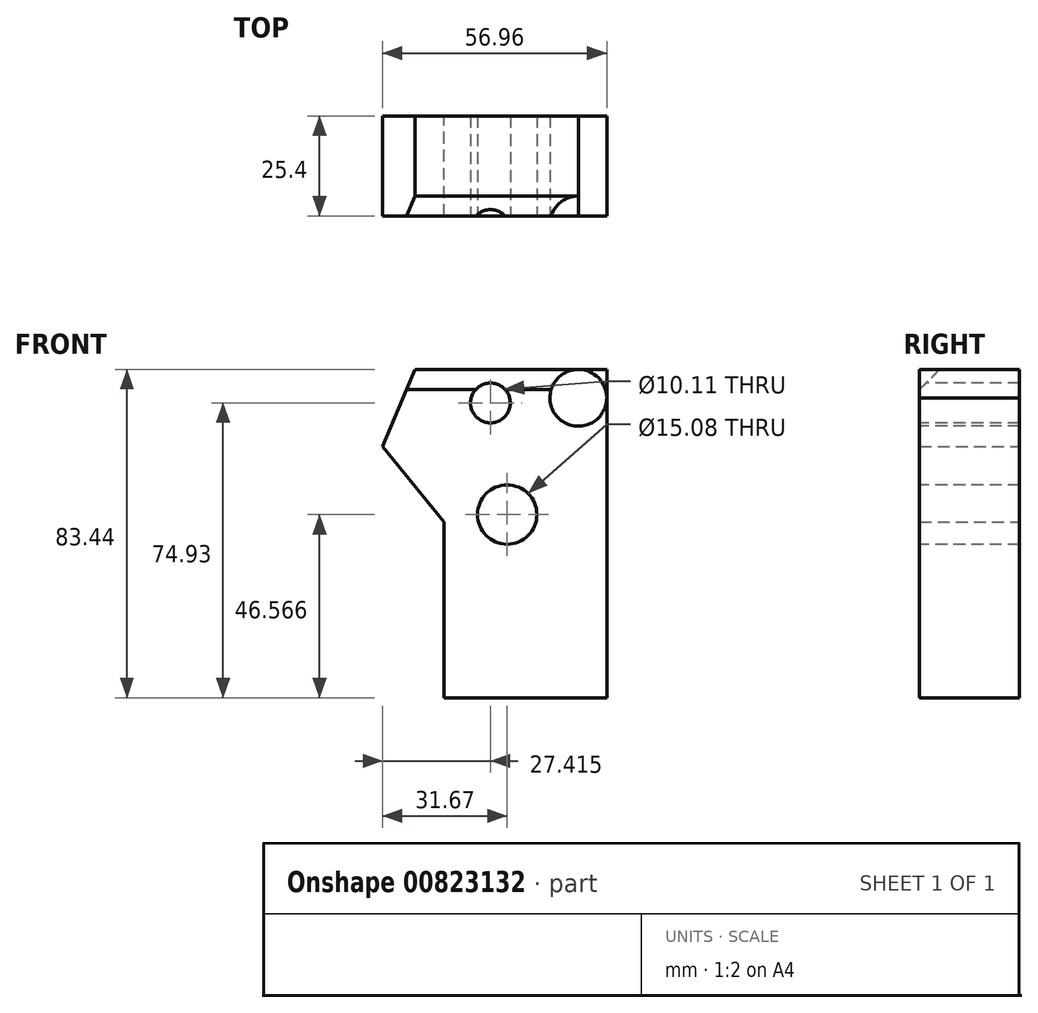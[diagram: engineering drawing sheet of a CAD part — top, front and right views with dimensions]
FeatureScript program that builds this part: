
annotation { "Feature Type Name" : "Feature", "Feature Type Description" : "" }
export const myFeature = defineFeature(function(context is Context, id is Id, definition is map)
    precondition{}
    {
        {
            var Q0;
            Q0=qCreatedBy(makeId("Front.planeOp"),FACE);
            var sketch = newSketch(context, id + "F0", { "sketchPlane" : qUnion([Q0])});
            skLineSegment(sketch, "E0", {"start": v(-32.51, 53.42) * mm, "end": v(-40.77, 33.8) * mm});
            skLineSegment(sketch, "E1", {"start": v(-40.77, 33.8) * mm, "end": v(-25.17, 14.7) * mm});
            skLineSegment(sketch, "E2", {"start": v(-25.17, 14.7) * mm, "end": v(-25.17, -30.02) * mm});
            skLineSegment(sketch, "E3", {"start": v(-25.17, -30.02) * mm, "end": v(16.2, -30.02) * mm});
            skLineSegment(sketch, "E4", {"start": v(16.2, -30.02) * mm, "end": v(16.2, 53.42) * mm});
            skLineSegment(sketch, "E5", {"start": v(-32.51, 53.42) * mm, "end": v(16.2, 53.42) * mm});
            skSolve(sketch);
        }
        {
            var Q0;
            Q0=makeQuery(id+"F0.imprint","IMPRINT",FACE,{"disambiguationData":[TD([[makeQuery(id+"F0.imprint","IMPRINT",EDGE,{"derivedFrom":sQuery(id+"F0.wireOp",EDGE,"E0")}),1.0]])]});
            extrude(context, id + "F1", {"entities" : qUnion([Q0]), "depth" : 25.4 * mm, "offsetDistance" : 25.4 * mm});
        }
        {
            var Q0;
            Q0=makeQuery(id+"F1.opExtrude","CAP_FACE",FACE,{"disambiguationData":[OSD([sQuery(id+"F0.wireOp",EDGE,"E0"),sQuery(id+"F0.wireOp",EDGE,"E1"),sQuery(id+"F0.wireOp",EDGE,"E2"),sQuery(id+"F0.wireOp",EDGE,"E3"),sQuery(id+"F0.wireOp",EDGE,"E4"),sQuery(id+"F0.wireOp",EDGE,"E5")])],"isStart":false});
            var sketch = newSketch(context, id + "F2", { "sketchPlane" : qUnion([Q0])});
            skSolve(sketch);
        }
        {
            var Q0;
            Q0=makeQuery(id+"F2.imprint","IMPRINT",FACE,{"disambiguationData":[TD([[makeQuery(id+"F2.imprint","IMPRINT",EDGE,{"derivedFrom":makeQuery(id+"F1.opExtrude","CAP_EDGE",EDGE,{"disambiguationData":[OSD([sQuery(id+"F0.wireOp",EDGE,"E0")])],"isStart":false})}),1.0]])]});
            var sketch = newSketch(context, id + "F3", { "sketchPlane" : qUnion([Q0])});
            skCircle(sketch, "E6", {"center": v(-9.1, 16.55) * mm, "radius": 7.54 * mm});
            skCircle(sketch, "E7", {"center": v(-13.35, 44.9) * mm, "radius": 5.05 * mm});
            skCircle(sketch, "E8", {"center": v(8.98, 46.2) * mm, "radius": 7.22 * mm});
            skSolve(sketch);
        }
        {
            var Q0;
            Q0 = qSketchRegion(id + "F3", true);
            extrude(context, id + "F4", {"entities" : qUnion([Q0]), "operationType" : NewBodyOperationType.REMOVE, "oppositeDirection" : true, "depth" : 25.4 * mm, "offsetDistance" : 25.4 * mm});
        }
        {
            var Q0;
            {var subQ0=sQuery(id+"F0.wireOp",EDGE,"E0");var subQ1=sQuery(id+"F0.wireOp",EDGE,"E5");Q0=makeQuery(id+"F4.boolean.opBoolean","SPLIT",EDGE,{"disambiguationData":[TD([makeQuery(id+"F1.opExtrude","SWEPT_FACE",FACE,{"disambiguationData":[OSD([subQ0])]})])],"derivedFrom":makeQuery(id+"F1.opExtrude","CAP_EDGE",EDGE,{"disambiguationData":[OSD([subQ1])],"isStart":false})});}
            chamfer(context, id + "F5", {"entities" : qUnion([Q0]), "width" : 5.08 * mm, "tangentPropagation" : true});
        }
    });
